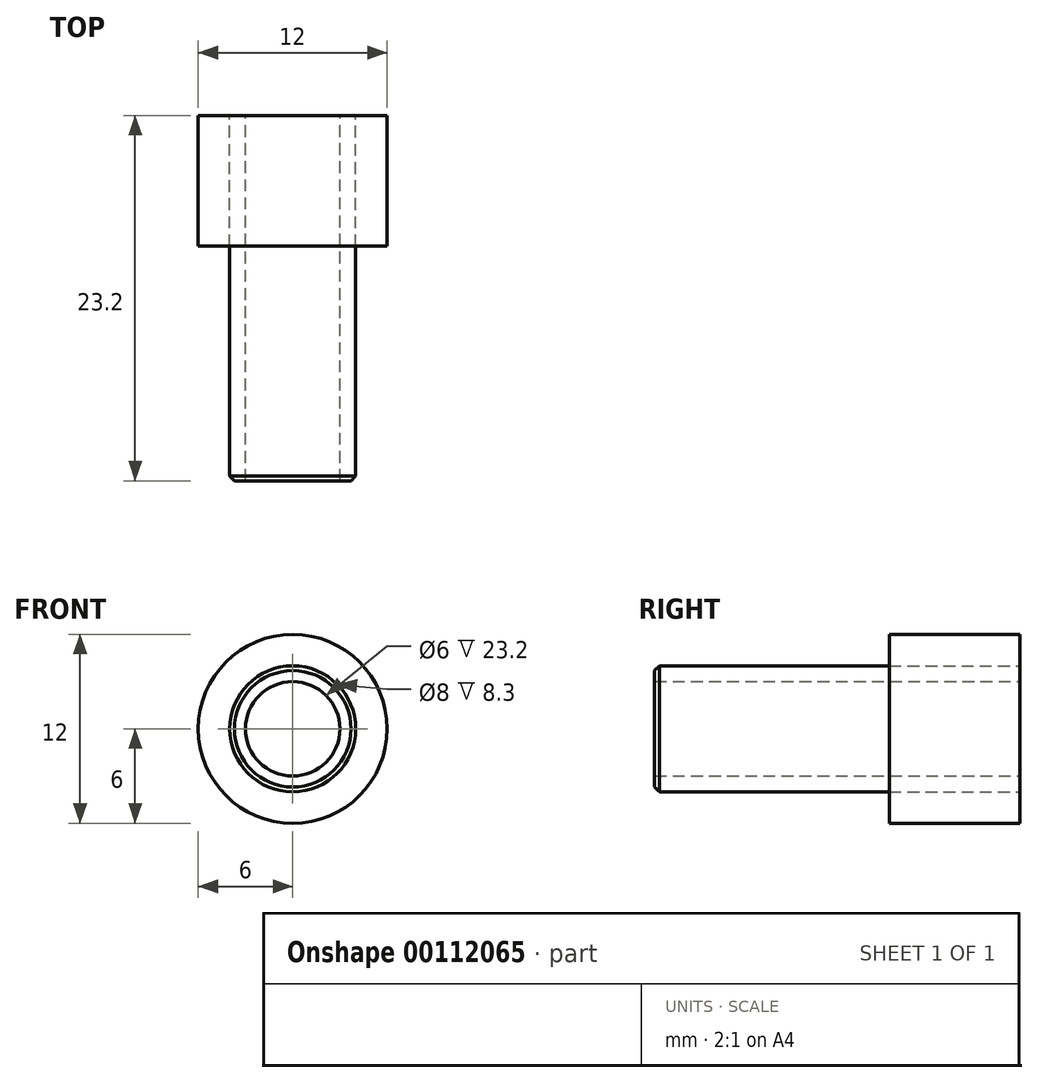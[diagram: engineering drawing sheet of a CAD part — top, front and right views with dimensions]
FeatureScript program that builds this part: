
annotation { "Feature Type Name" : "Feature", "Feature Type Description" : "" }
export const myFeature = defineFeature(function(context is Context, id is Id, definition is map)
    precondition{}
    {
        {
            var Q0;
            Q0=qCreatedBy(makeId("Front.planeOp"),FACE);
            var sketch = newSketch(context, id + "F0", { "sketchPlane" : qUnion([Q0])});
            skCircle(sketch, "E0", {"center": v(0, 0) * mm, "radius": 3 * mm});
            skCircle(sketch, "E1", {"center": v(0, 0) * mm, "radius": 4 * mm});
            skCircle(sketch, "E2", {"center": v(0, 0) * mm, "radius": 6 * mm});
            skSolve(sketch);
        }
        {
            var Q0;
            Q0=makeQuery(id+"F0.imprint","IMPRINT",FACE,{"disambiguationData":[TD([[makeQuery(id+"F0.imprint","IMPRINT",EDGE,{"derivedFrom":sQuery(id+"F0.wireOp",EDGE,"E1")}),-1.0]])]});
            extrude(context, id + "F1", {"entities" : qUnion([Q0]), "depth" : 8.3 * mm});
        }
        {
            var Q0;
            Q0=makeQuery(id+"F0.imprint","IMPRINT",FACE,{"disambiguationData":[TD([[makeQuery(id+"F0.imprint","IMPRINT",EDGE,{"derivedFrom":sQuery(id+"F0.wireOp",EDGE,"E0")}),-1.0]])]});
            extrude(context, id + "F2", {"entities" : qUnion([Q0]), "depth" : 23.2 * mm});
        }
        {
            var Q0;
            Q0=makeQuery(id+"F2.opExtrude","CAP_EDGE",EDGE,{"disambiguationData":[OSD([sQuery(id+"F0.wireOp",EDGE,"E1")])],"isStart":false});
            chamfer(context, id + "F3", {"entities" : qUnion([Q0]), "width" : 0.3 * mm, "tangentPropagation" : true});
        }
    });
